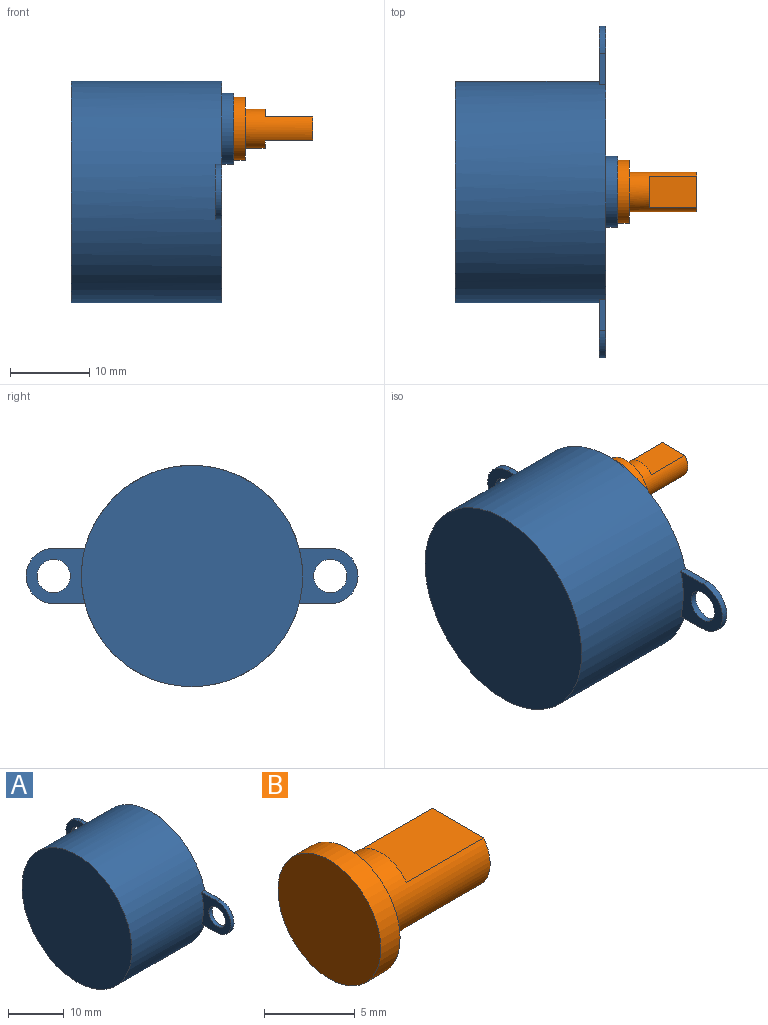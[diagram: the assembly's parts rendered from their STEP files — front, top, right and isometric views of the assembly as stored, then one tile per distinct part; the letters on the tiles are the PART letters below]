
ASSEMBLY  parts=2 mates=1
PART A: 17 faces, bbox 20.5x42x28 mm
  f0: cylinder r=14mm len=28mm, axis (-1,0,0), area 1660mm2, adj f1,f2,f3,f5,f7,f9,f11,f12
  f1: plane 42x28mm, normal (1,0,0), area 614mm2, adj f0,f3,f4,f5,f6,f8,f9,f10
  f2: plane 28x28mm, normal (-1,0,0), area 615.8mm2, adj f0
  f3: plane 3.94x0.8mm, normal (0,0,1), area 3.2mm2, adj f0,f1,f4,f7
  f4: cylinder r=3.5mm len=7mm, axis (1,0,0), area 8.8mm2, adj f1,f3,f5,f7
  f5: plane 3.94x0.8mm, normal (0,0,-1), area 3.2mm2, adj f0,f1,f4,f7
  f6: cylinder r=2.1mm len=4.2mm, axis (1,0,0), area 10.6mm2, adj f1,f7
  f7: plane 7.44x7mm, normal (-1,0,0), area 30.9mm2, adj f0,f3,f4,f5,f6
  f8: cylinder r=3.5mm len=7mm, axis (1,0,0), area 8.8mm2, adj f1,f9,f11,f12
  f9: plane 3.94x0.8mm, normal (0,0,1), area 3.2mm2, adj f0,f1,f8,f12
  f10: cylinder r=2.1mm len=4.2mm, axis (1,0,0), area 10.6mm2, adj f1,f12
  f11: plane 3.94x0.8mm, normal (0,0,-1), area 3.2mm2, adj f0,f1,f8,f12
  f12: plane 7.44x7mm, normal (-1,0,0), area 30.9mm2, adj f0,f8,f9,f10,f11
  f13: cylinder r=4mm len=8mm, axis (-1,0,0), area 37.7mm2, adj f15,f16
  f14: cylinder r=4.5mm len=9mm, axis (-1,0,0), area 42.4mm2, adj f1,f15
  f15: plane 9x9mm, normal (1,0,0), area 13.4mm2, adj f13,f14
  f16: plane 8x8mm, normal (1,0,0), area 50.3mm2, adj f13
PART B: 9 faces, bbox 10x8x8 mm
  f0: plane 4x1mm, normal (1,0,0), area 2.8mm2, adj f1,f4
  f1: cylinder r=2.5mm len=8.5mm, axis (-1,0,0), area 77.9mm2, adj f0,f2,f3,f4,f5,f7
  f2: plane 4x1mm, normal (1,0,0), area 2.8mm2, adj f1,f3
  f3: plane 6x4mm, normal (0,0,1), area 24mm2, adj f1,f2,f5
  f4: plane 6x4mm, normal (0,0,-1), area 24mm2, adj f0,f1,f5
  f5: plane 5x3mm, normal (1,0,0), area 14mm2, adj f1,f3,f4
  f6: cylinder r=4mm len=8mm, axis (-1,0,0), area 37.7mm2, adj f7,f8
  f7: plane 8x8mm, normal (1,0,0), area 30.6mm2, adj f1,f6
  f8: plane 8x8mm, normal (-1,0,0), area 50.3mm2, adj f6
PLACE A t=(-1.8,-3.86,-2.77)mm fixed
PLACE B rot(axis=(-1,0,0),179.8deg) t=(18.7,-3.75,-22.74)mm
MATE revolute B.f1 <-> A.f13  axis (-1,0,0) through (18.7,-3.86,5.23)mm
